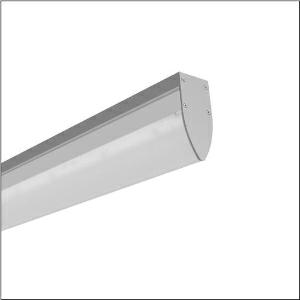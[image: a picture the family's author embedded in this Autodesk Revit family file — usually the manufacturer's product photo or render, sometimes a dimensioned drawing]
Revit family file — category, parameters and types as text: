
# Revit family: mira_r__21_td_51fr527p454a_1793
name_source: partatom
category: Lighting Fixtures
units: mm (PartAtom-declared; Revit-internal decimal feet)

## family parameters
Cut with Voids When Loaded = No
Host = Face
Light Source = No
Part Type = Normal
Room Calculation Point = No
Round Connector Dimension = Use Diameter
Shared = No

## types (1)
- Mira® 21 TD (1 x LED, 5040 lm, 34 W, 4000K)
    Apparent Load = 34 VA
    CIE Flux Codes = 40 68 87 81 100
    Color Rendering = 80
    Color Temperature = 4000K
    Default Elevation = 1800 mm
    Description = Mira® 21 TD, clean room luminaire, primary light control with reflector, primary optical cover: cover, of PMMA, frosted, light emission: direct distribution, primary light characteristic: symmetric, installation type: surface-mounted, LED, rated luminous flux: 5.040lm, luminous efficacy: 148lm/W, light colour: 840, colour temperature: 4000K, control gear: ECG, with terminal, 3-pole, max. 2.5mm², mains connection: 230V, AC, 50/60Hz, rated input power: 34W, luminaire housing, of sheet steel, coated, pure white (RAL 9010), length: 1.500mm, width: 55mm, height: 120mm, protection rating (complete): IP43, insulation class (complete): insulation class I (protective earthing), certification: CE, UKCA, permissible operating ambient temperature: -5..+40°C, standard: EN 50419, packaging unit: 1 piece
    Height = 0 mm  [stored 0 ft]
    Lamp = 1 x LED
    Lamp Light Flux = 5040 lm
    Lamp Power = 34 W
    Lamp count = 1
    Length = 1500 mm
    Luminous efficacy = 148 lm/W
    Manufacturer = Siteco
    ModVariant = No
    Model = 51FR527P454A
    Mounting Place = Ceiling
    Mounting Type = Recessed
    Number of Poles = 1
    OnlyDefault = Yes
    Power Factor = 1
    Product Name = Mira® 21 TD
    Product group = clean room luminaire
    ProductGroupID = 402
    Protection Class = Protection class I
    Protection Degree = IP 43
    RLX_Detail_Level = 1
    RLX_Emergency_Light_Flux = 0 lm
    RLX_Emergency_Type = 0
    RLX_Emergency_Type_DB = No
    RlxData = <blob elided: 25185 chars, md5=cd6f5be4>
    Socket = socket
    Standby Power = 0 W
    System Light Flux = 5040 lm
    System Power = 34 W
    Type Comments = Product without accessories
    Type Image = l_1007115.jpg
    URL = http://relux.com
    VarID = ---
    Voltage = 0 V
    Weight = 0.00 kg
    Width = 55 mm

note: [stored X ft] marks values corroborated as IEEE doubles in the binary element streams (Revit-internal decimal feet)

## geometry (parser evidence)
native form markers: Blend x4, Sweep x14
no freeform markers — native parametric forms only
